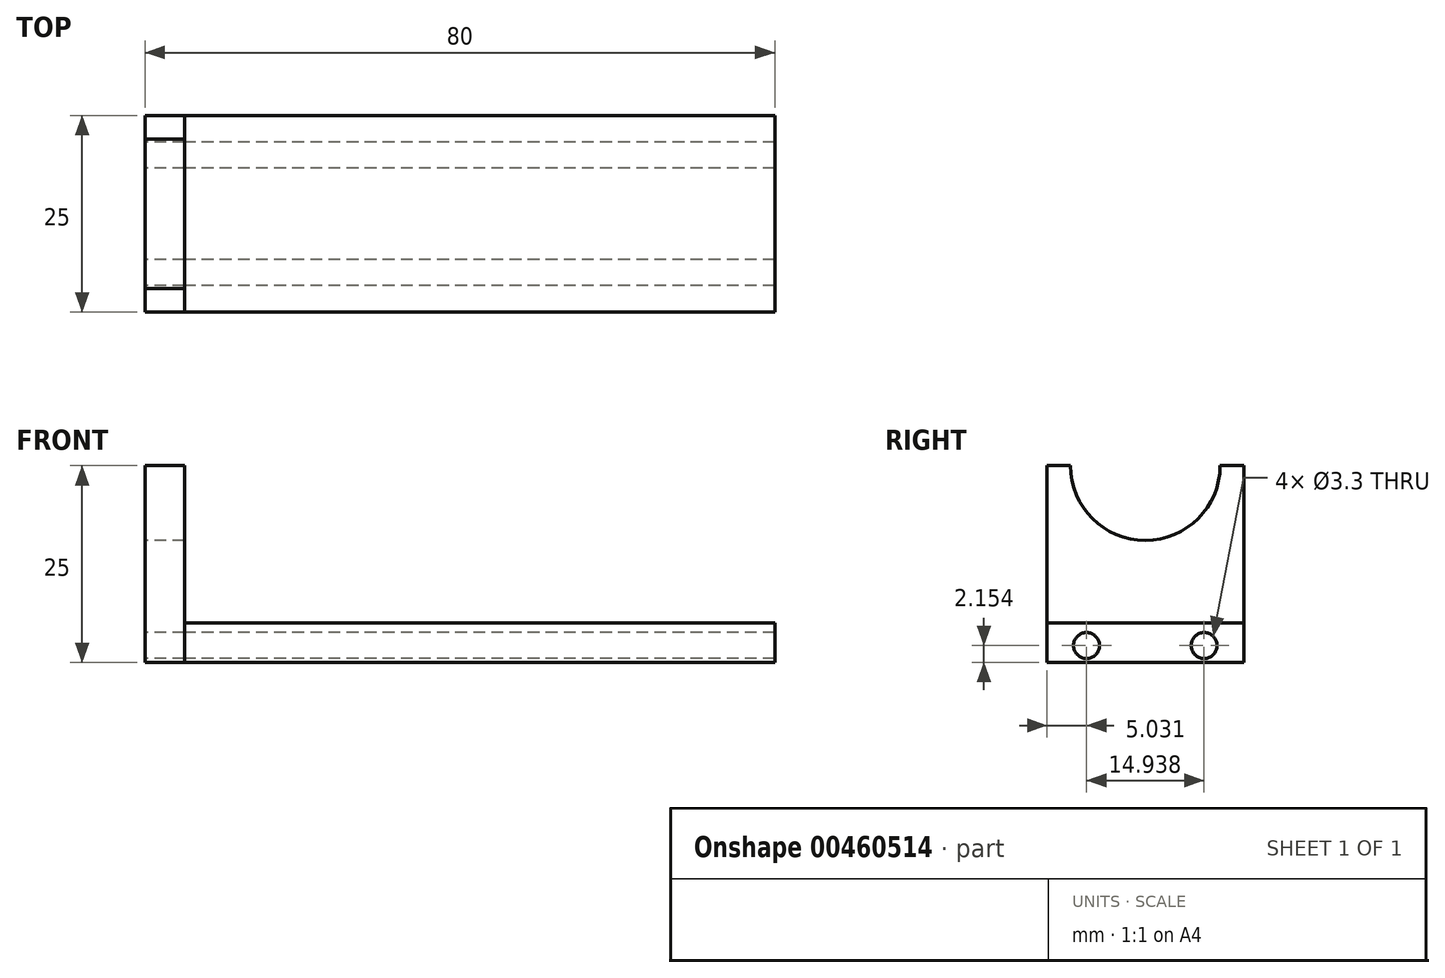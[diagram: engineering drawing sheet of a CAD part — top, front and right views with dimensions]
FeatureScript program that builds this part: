
annotation { "Feature Type Name" : "Feature", "Feature Type Description" : "" }
export const myFeature = defineFeature(function(context is Context, id is Id, definition is map)
    precondition{}
    {
        {
            var Q0;
            Q0=qCreatedBy(makeId("Top.planeOp"),FACE);
            var sketch = newSketch(context, id + "F0", { "sketchPlane" : qUnion([Q0])});
            skLineSegment(sketch, "E0.bottom", {"start": v(37.5, 12.5) * mm, "end": v(-37.5, 12.5) * mm});
            skLineSegment(sketch, "E0.top", {"start": v(37.5, -12.5) * mm, "end": v(-37.5, -12.5) * mm});
            skLineSegment(sketch, "E0.left", {"start": v(37.5, 12.5) * mm, "end": v(37.5, -12.5) * mm});
            skLineSegment(sketch, "E0.right", {"start": v(-37.5, 12.5) * mm, "end": v(-37.5, -12.5) * mm});
            skPoint(sketch, "E0.middle", {"position": v(0, 0) * mm});
            skSolve(sketch);
        }
        {
            var Q0;
            Q0 = qSketchRegion(id + "F0", true);
            extrude(context, id + "F1", {"entities" : qUnion([Q0]), "depth" : 5 * mm});
        }
        {
            var Q0;
            Q0=makeQuery(id+"F1.opExtrude","SWEPT_FACE",FACE,{"disambiguationData":[OSD([sQuery(id+"F0.wireOp",EDGE,"E0.right")])]});
            var sketch = newSketch(context, id + "F2", { "sketchPlane" : qUnion([Q0])});
            skLineSegment(sketch, "E1.bottom", {"start": v(-12.5, 0) * mm, "end": v(12.5, 0) * mm});
            skLineSegment(sketch, "E1.top", {"start": v(-12.5, 25) * mm, "end": v(12.5, 25) * mm});
            skLineSegment(sketch, "E1.left", {"start": v(-12.5, 0) * mm, "end": v(-12.5, 25) * mm});
            skLineSegment(sketch, "E1.right", {"start": v(12.5, 0) * mm, "end": v(12.5, 25) * mm});
            skSolve(sketch);
        }
        {
            var Q0;
            Q0 = qSketchRegion(id + "F2", true);
            extrude(context, id + "F3", {"entities" : qUnion([Q0]), "depth" : 5 * mm});
        }
        {
            var Q0;
            Q0=makeQuery(id+"F3.opExtrude","CAP_FACE",FACE,{"disambiguationData":[OSD([sQuery(id+"F2.wireOp",EDGE,"E1.bottom"),sQuery(id+"F2.wireOp",EDGE,"E1.top"),sQuery(id+"F2.wireOp",EDGE,"E1.left"),sQuery(id+"F2.wireOp",EDGE,"E1.right")])],"isStart":false});
            var sketch = newSketch(context, id + "F4", { "sketchPlane" : qUnion([Q0])});
            skCircle(sketch, "E2", {"center": v(0, 25) * mm, "radius": 9.5 * mm});
            skPoint(sketch, "E3", {"position": v(-7.47, 2.15) * mm});
            skPoint(sketch, "E4.MirrorP", {"position": v(7.47, 2.15) * mm});
            skSolve(sketch);
        }
        {
            var Q0;
            Q0 = qSketchRegion(id + "F4", true);
            extrude(context, id + "F5", {"entities" : qUnion([Q0]), "operationType" : NewBodyOperationType.REMOVE, "oppositeDirection" : true, "depth" : 25 * mm});
        }
        {
            var Q0;
            Q0=sQuery(id+"F4.wireOp",VERTEX,"E3");
            var Q1;
            Q1=sQuery(id+"F4.wireOp",VERTEX,"E4.MirrorP");
            var Q2;
            Q2=makeQuery(id+"F3.opExtrude","SWEPT_BODY",BODY,{"disambiguationData":[OSD([sQuery(id+"F2.wireOp",EDGE,"E1.bottom"),sQuery(id+"F2.wireOp",EDGE,"E1.top"),sQuery(id+"F2.wireOp",EDGE,"E1.left"),sQuery(id+"F2.wireOp",EDGE,"E1.right")])]});
            var Q3;
            Q3=makeQuery(id+"F1.opExtrude","SWEPT_BODY",BODY,{"disambiguationData":[OSD([sQuery(id+"F0.wireOp",EDGE,"E0.bottom"),sQuery(id+"F0.wireOp",EDGE,"E0.top"),sQuery(id+"F0.wireOp",EDGE,"E0.left"),sQuery(id+"F0.wireOp",EDGE,"E0.right")])]});
            hole(context, id + "F6", {"style" : HoleStyle.SIMPLE, "endStyle" : HoleEndStyle.THROUGH, "standardTappedOrClearance" : lookupTablePath({ "standard" : "ISO", "fit" : "Normal", "size" : "M3", "type" : "Clearance" }), "standardBlindInLast" : lookupTablePath({ "fit" : "Standard", "standard" : "ISO", "size" : "M3", "type" : "Clearance" }), "holeDiameter" : 3.3 * mm, "isTappedThrough" : true, "tappedDepth" : 12 * mm, "tapClearance" : 3, "startFromSketch" : true, "locations" : qUnion([Q0, Q1]), "scope" : qUnion([Q2, Q3])});
        }
    });
